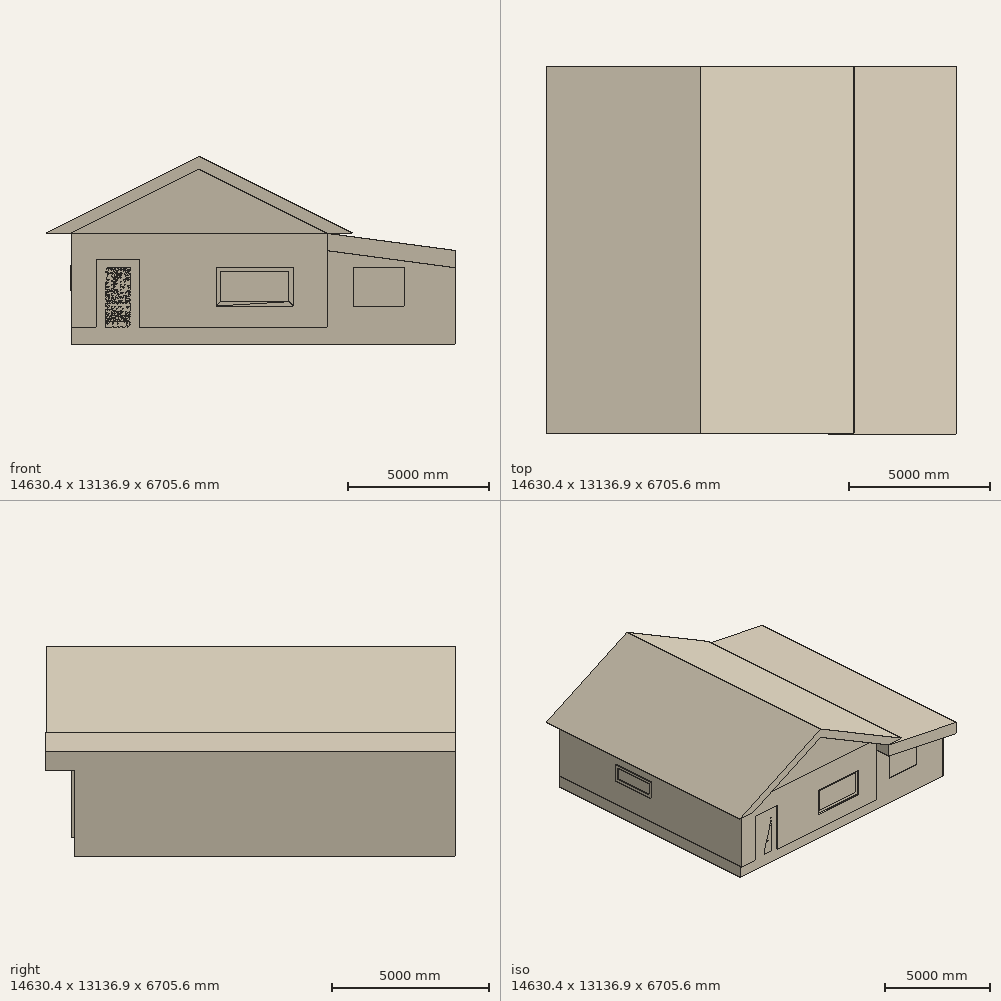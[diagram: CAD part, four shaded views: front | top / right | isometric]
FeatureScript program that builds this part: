
annotation { "Feature Type Name" : "Feature", "Feature Type Description" : "" }
export const myFeature = defineFeature(function(context is Context, id is Id, definition is map)
    precondition{}
    {
        {
            var Q0;
            Q0=qCreatedBy(makeId("Front.planeOp"),FACE);
            var sketch = newSketch(context, id + "F0", { "sketchPlane" : qUnion([Q0])});
            skLineSegment(sketch, "E0", {"start": v(0, 0) * mm, "end": v(-4572, 0) * mm});
            skLineSegment(sketch, "E1", {"start": v(0, 0) * mm, "end": v(4572, 0) * mm});
            skLineSegment(sketch, "E2", {"start": v(0, 0) * mm, "end": v(0, 2286) * mm});
            skLineSegment(sketch, "E3", {"start": v(-4572, 0) * mm, "end": v(0, 2286) * mm});
            skLineSegment(sketch, "E4", {"start": v(4572, 0) * mm, "end": v(0, 2286) * mm});
            skLineSegment(sketch, "E5", {"start": v(-4572, 0) * mm, "end": v(-5486.4, 0) * mm});
            skLineSegment(sketch, "E6", {"start": v(4572, 0) * mm, "end": v(5486.4, 0) * mm});
            skLineSegment(sketch, "E7", {"start": v(0, 2286) * mm, "end": v(0, 2743.2) * mm});
            skLineSegment(sketch, "E8", {"start": v(-5486.4, 0) * mm, "end": v(0, 2743.2) * mm});
            skLineSegment(sketch, "E9", {"start": v(5486.4, 0) * mm, "end": v(0, 2743.2) * mm});
            skLineSegment(sketch, "E10", {"start": v(-4572, 0) * mm, "end": v(-4572, -3352.8) * mm});
            skLineSegment(sketch, "E11", {"start": v(-4572, -3352.8) * mm, "end": v(4572, -3352.8) * mm});
            skLineSegment(sketch, "E12", {"start": v(4572, 0) * mm, "end": v(4572, -3352.8) * mm});
            skLineSegment(sketch, "E13", {"start": v(-4572, -3352.8) * mm, "end": v(-4572, -3962.4) * mm});
            skLineSegment(sketch, "E14", {"start": v(-4572, -3962.4) * mm, "end": v(4572, -3962.4) * mm});
            skLineSegment(sketch, "E15", {"start": v(4572, -3352.8) * mm, "end": v(4572, -3962.4) * mm});
            skLineSegment(sketch, "E16", {"start": v(4572, -3962.4) * mm, "end": v(9144, -3962.4) * mm});
            skLineSegment(sketch, "E17", {"start": v(4572, -3352.8) * mm, "end": v(9144, -3352.8) * mm});
            skLineSegment(sketch, "E18", {"start": v(9144, -3352.8) * mm, "end": v(9144, -3962.4) * mm});
            skLineSegment(sketch, "E19", {"start": v(9144, -3352.8) * mm, "end": v(9144, -609.6) * mm});
            skLineSegment(sketch, "E20", {"start": v(4572, 0) * mm, "end": v(9144, -609.6) * mm});
            skLineSegment(sketch, "E21", {"start": v(4572, -615) * mm, "end": v(9144, -1224.6) * mm});
            skLineSegment(sketch, "E22", {"start": v(-3352.8, -3352.8) * mm, "end": v(-3352.8, -1219.2) * mm});
            skLineSegment(sketch, "E23", {"start": v(-3352.8, -1219.2) * mm, "end": v(-2438.4, -1219.2) * mm});
            skLineSegment(sketch, "E24", {"start": v(-2438.4, -1219.2) * mm, "end": v(-2438.4, -3352.8) * mm});
            skLineSegment(sketch, "E25.0", {"start": v(-2133.6, -914.4) * mm, "end": v(-2133.6, -3352.8) * mm});
            skLineSegment(sketch, "E25.1", {"start": v(-3657.6, -914.4) * mm, "end": v(-2133.6, -914.4) * mm});
            skLineSegment(sketch, "E25.2", {"start": v(-3657.6, -3352.8) * mm, "end": v(-3657.6, -914.4) * mm});
            skLineSegment(sketch, "E26.bottom", {"start": v(606.8, -1219.2) * mm, "end": v(3350, -1219.2) * mm});
            skLineSegment(sketch, "E26.top", {"start": v(606.8, -2590.8) * mm, "end": v(3350, -2590.8) * mm});
            skLineSegment(sketch, "E26.left", {"start": v(606.8, -1219.2) * mm, "end": v(606.8, -2590.8) * mm});
            skLineSegment(sketch, "E26.right", {"start": v(3350, -1219.2) * mm, "end": v(3350, -2590.8) * mm});
            skLineSegment(sketch, "E27.bottom", {"start": v(5499.78, -1219.2) * mm, "end": v(7329.49, -1219.2) * mm});
            skLineSegment(sketch, "E27.top", {"start": v(5499.78, -2590.8) * mm, "end": v(7329.49, -2590.8) * mm});
            skLineSegment(sketch, "E27.left", {"start": v(5499.78, -1219.2) * mm, "end": v(5499.78, -2590.8) * mm});
            skLineSegment(sketch, "E27.right", {"start": v(7329.49, -1219.2) * mm, "end": v(7329.49, -2590.8) * mm});
            skLineSegment(sketch, "E28.0", {"start": v(759.2, -1371.6) * mm, "end": v(3197.6, -1371.6) * mm});
            skLineSegment(sketch, "E28.1", {"start": v(759.2, -1371.6) * mm, "end": v(759.2, -2438.4) * mm});
            skLineSegment(sketch, "E28.2", {"start": v(759.2, -2438.4) * mm, "end": v(3197.6, -2438.4) * mm});
            skLineSegment(sketch, "E28.3", {"start": v(3197.6, -1371.6) * mm, "end": v(3197.6, -2438.4) * mm});
            skSolve(sketch);
        }
        {
            var Q0;
            Q0=makeQuery(id+"F0.imprint","IMPRINT",FACE,{"disambiguationData":[TD([[makeQuery(id+"F0.imprint","IMPRINT",EDGE,{"derivedFrom":sQuery(id+"F0.wireOp",EDGE,"E3")}),1.0]])]});
            var Q1;
            Q1=makeQuery(id+"F0.imprint","IMPRINT",FACE,{"disambiguationData":[TD([[makeQuery(id+"F0.imprint","IMPRINT",EDGE,{"derivedFrom":sQuery(id+"F0.wireOp",EDGE,"E4")}),-1.0]])]});
            var Q2;
            {var subQ0=sQuery(id+"F0.wireOp",EDGE,"E20");Q2=makeQuery(id+"F0.imprint","IMPRINT",FACE,{"disambiguationData":[TD([[makeQuery(id+"F0.imprint","IMPRINT",EDGE,{"derivedFrom":subQ0}),-1.0]])]});}
            extrude(context, id + "F1", {"entities" : qUnion([Q0, Q1, Q2]), "depth" : 914.4 * mm, "offsetDistance" : 30.48 * mm, "hasSecondDirection" : true, "secondDirectionOppositeDirection" : true, "secondDirectionDepth" : 12192 * mm});
        }
        {
            var Q0;
            Q0=makeQuery(id+"F0.imprint","IMPRINT",FACE,{"disambiguationData":[TD([[makeQuery(id+"F0.imprint","IMPRINT",EDGE,{"derivedFrom":sQuery(id+"F0.wireOp",EDGE,"E0")}),-1.0]])]});
            var Q1;
            Q1=makeQuery(id+"F0.imprint","IMPRINT",FACE,{"disambiguationData":[TD([[makeQuery(id+"F0.imprint","IMPRINT",EDGE,{"derivedFrom":sQuery(id+"F0.wireOp",EDGE,"E1")}),1.0]])]});
            extrude(context, id + "F2", {"entities" : qUnion([Q0, Q1]), "operationType" : NewBodyOperationType.ADD, "depth" : 152.4 * mm, "offsetDistance" : 30.48 * mm, "hasSecondDirection" : true, "secondDirectionOppositeDirection" : true, "secondDirectionDepth" : 11277.6 * mm});
        }
        {
            var Q0;
            Q0=makeQuery(id+"F0.imprint","IMPRINT",FACE,{"disambiguationData":[TD([[makeQuery(id+"F0.imprint","IMPRINT",EDGE,{"derivedFrom":sQuery(id+"F0.wireOp",EDGE,"E26.bottom")}),-1.0]])]});
            var Q1;
            {var subQ0=sQuery(id+"F0.wireOp",EDGE,"E22");Q1=makeQuery(id+"F0.imprint","IMPRINT",FACE,{"disambiguationData":[TD([[makeQuery(id+"F0.imprint","IMPRINT",EDGE,{"derivedFrom":subQ0}),-1.0]])]});}
            var Q2;
            {var subQ0=sQuery(id+"F0.wireOp",EDGE,"E20");Q2=makeQuery(id+"F0.imprint","IMPRINT",FACE,{"disambiguationData":[TD([[makeQuery(id+"F0.imprint","IMPRINT",EDGE,{"derivedFrom":subQ0}),-1.0]])]});}
            var Q3;
            Q3=makeQuery(id+"F0.imprint","IMPRINT",FACE,{"disambiguationData":[TD([[makeQuery(id+"F0.imprint","IMPRINT",EDGE,{"derivedFrom":sQuery(id+"F0.wireOp",EDGE,"E15")}),1.0]])]});
            var Q4;
            {var subQ0=sQuery(id+"F0.wireOp",EDGE,"E22");Q4=makeQuery(id+"F0.imprint","IMPRINT",FACE,{"disambiguationData":[TD([[makeQuery(id+"F0.imprint","IMPRINT",EDGE,{"derivedFrom":subQ0}),1.0]])]});}
            var Q5;
            {var subQ0=sQuery(id+"F0.wireOp",EDGE,"E17");Q5=makeQuery(id+"F0.imprint","IMPRINT",FACE,{"disambiguationData":[TD([[makeQuery(id+"F0.imprint","IMPRINT",EDGE,{"derivedFrom":subQ0}),1.0]])]});}
            var Q6;
            {var subQ5=sQuery(id+"F0.wireOp",EDGE,"E13");Q6=makeQuery(id+"F0.imprint","IMPRINT",FACE,{"disambiguationData":[TD([[makeQuery(id+"F0.imprint","IMPRINT",EDGE,{"derivedFrom":subQ5}),1.0]])]});}
            var Q7;
            Q7=makeQuery(id+"F1.opExtrude","CAP_FACE",FACE,{"disambiguationData":[OSD([sQuery(id+"F0.wireOp",EDGE,"E12"),sQuery(id+"F0.wireOp",EDGE,"E19"),sQuery(id+"F0.wireOp",EDGE,"E20"),sQuery(id+"F0.wireOp",EDGE,"E21")])],"isStart":false});
            extrude(context, id + "F3", {"entities" : qUnion([Q0, Q1, Q2, Q3, Q4, Q5, Q6, Q7]), "operationType" : NewBodyOperationType.ADD, "depth" : 30.48 * mm, "offsetDistance" : 30.48 * mm, "hasSecondDirection" : true, "secondDirectionOppositeDirection" : true, "secondDirectionDepth" : 12192 * mm});
        }
        {
            var Q0;
            Q0=makeQuery(id+"F0.imprint","IMPRINT",FACE,{"disambiguationData":[TD([[makeQuery(id+"F0.imprint","IMPRINT",EDGE,{"derivedFrom":sQuery(id+"F0.wireOp",EDGE,"E0")}),1.0]])]});
            extrude(context, id + "F4", {"entities" : qUnion([Q0]), "depth" : 121.92 * mm, "offsetDistance" : 30.48 * mm, "hasSecondDirection" : true, "secondDirectionOppositeDirection" : true, "secondDirectionDepth" : 12192 * mm});
        }
        {
            var Q0;
            {var subQ0=sQuery(id+"F0.wireOp",EDGE,"E22");Q0=makeQuery(id+"F0.imprint","IMPRINT",FACE,{"disambiguationData":[TD([[makeQuery(id+"F0.imprint","IMPRINT",EDGE,{"derivedFrom":subQ0}),-1.0]])]});}
            var Q1;
            Q1=makeQuery(id+"F0.imprint","IMPRINT",FACE,{"disambiguationData":[TD([[makeQuery(id+"F0.imprint","IMPRINT",EDGE,{"derivedFrom":sQuery(id+"F0.wireOp",EDGE,"E26.bottom")}),-1.0]])]});
            extrude(context, id + "F5", {"entities" : qUnion([Q0, Q1]), "depth" : 30.48 * mm, "offsetDistance" : 30.48 * mm});
        }
        {
            var Q0;
            Q0=makeQuery(id+"F0.imprint","IMPRINT",FACE,{"disambiguationData":[TD([[makeQuery(id+"F0.imprint","IMPRINT",EDGE,{"derivedFrom":sQuery(id+"F0.wireOp",EDGE,"E26.bottom")}),-1.0]])]});
            var Q1;
            Q1=makeQuery(id+"F0.imprint","IMPRINT",FACE,{"disambiguationData":[TD([[makeQuery(id+"F0.imprint","IMPRINT",EDGE,{"derivedFrom":sQuery(id+"F0.wireOp",EDGE,"E27.bottom")}),-1.0]])]});
            extrude(context, id + "F6", {"entities" : qUnion([Q0, Q1]), "depth" : 30.48 * mm, "offsetDistance" : 30.48 * mm});
        }
        {
            var Q0;
            Q0=makeQuery(id+"F0.imprint","IMPRINT",FACE,{"disambiguationData":[TD([[makeQuery(id+"F0.imprint","IMPRINT",EDGE,{"derivedFrom":sQuery(id+"F0.wireOp",EDGE,"E28.0")}),-1.0]])]});
            extrude(context, id + "F7", {"entities" : qUnion([Q0]), "depth" : 30.48 * mm, "offsetDistance" : 30.48 * mm});
        }
        {
            var Q0;
            Q0=makeQuery(id+"F4.opExtrude","SWEPT_FACE",FACE,{"disambiguationData":[OSD([sQuery(id+"F0.wireOp",EDGE,"E10")])]});
            var sketch = newSketch(context, id + "F8", { "sketchPlane" : qUnion([Q0])});
            skLineSegment(sketch, "E29.bottom", {"start": v(-8412.48, -1127.76) * mm, "end": v(-5974.08, -1127.76) * mm});
            skLineSegment(sketch, "E29.top", {"start": v(-8412.48, -2042.16) * mm, "end": v(-5974.08, -2042.16) * mm});
            skLineSegment(sketch, "E29.left", {"start": v(-8412.48, -1127.76) * mm, "end": v(-8412.48, -2042.16) * mm});
            skLineSegment(sketch, "E29.right", {"start": v(-5974.08, -1127.76) * mm, "end": v(-5974.08, -2042.16) * mm});
            skLineSegment(sketch, "E30.0", {"start": v(-8260.08, -1280.16) * mm, "end": v(-6126.48, -1280.16) * mm});
            skLineSegment(sketch, "E30.1", {"start": v(-8260.08, -1280.16) * mm, "end": v(-8260.08, -1889.76) * mm});
            skLineSegment(sketch, "E30.2", {"start": v(-8260.08, -1889.76) * mm, "end": v(-6126.48, -1889.76) * mm});
            skLineSegment(sketch, "E30.3", {"start": v(-6126.48, -1280.16) * mm, "end": v(-6126.48, -1889.76) * mm});
            skSolve(sketch);
        }
        {
            var Q0;
            Q0=makeQuery(id+"F8.imprint","IMPRINT",FACE,{"disambiguationData":[TD([[makeQuery(id+"F8.imprint","IMPRINT",EDGE,{"derivedFrom":sQuery(id+"F8.wireOp",EDGE,"E29.bottom")}),-1.0]])]});
            extrude(context, id + "F9", {"entities" : qUnion([Q0]), "operationType" : NewBodyOperationType.ADD, "depth" : 30.48 * mm, "offsetDistance" : 30.48 * mm});
        }
        {
            var Q0;
            Q0=makeQuery(id+"F8.imprint","IMPRINT",FACE,{"disambiguationData":[TD([[makeQuery(id+"F8.imprint","IMPRINT",EDGE,{"derivedFrom":sQuery(id+"F8.wireOp",EDGE,"E29.bottom")}),-1.0]])]});
            extrude(context, id + "F10", {"entities" : qUnion([Q0]), "operationType" : NewBodyOperationType.ADD, "depth" : 30.48 * mm, "offsetDistance" : 30.48 * mm});
        }
    });
